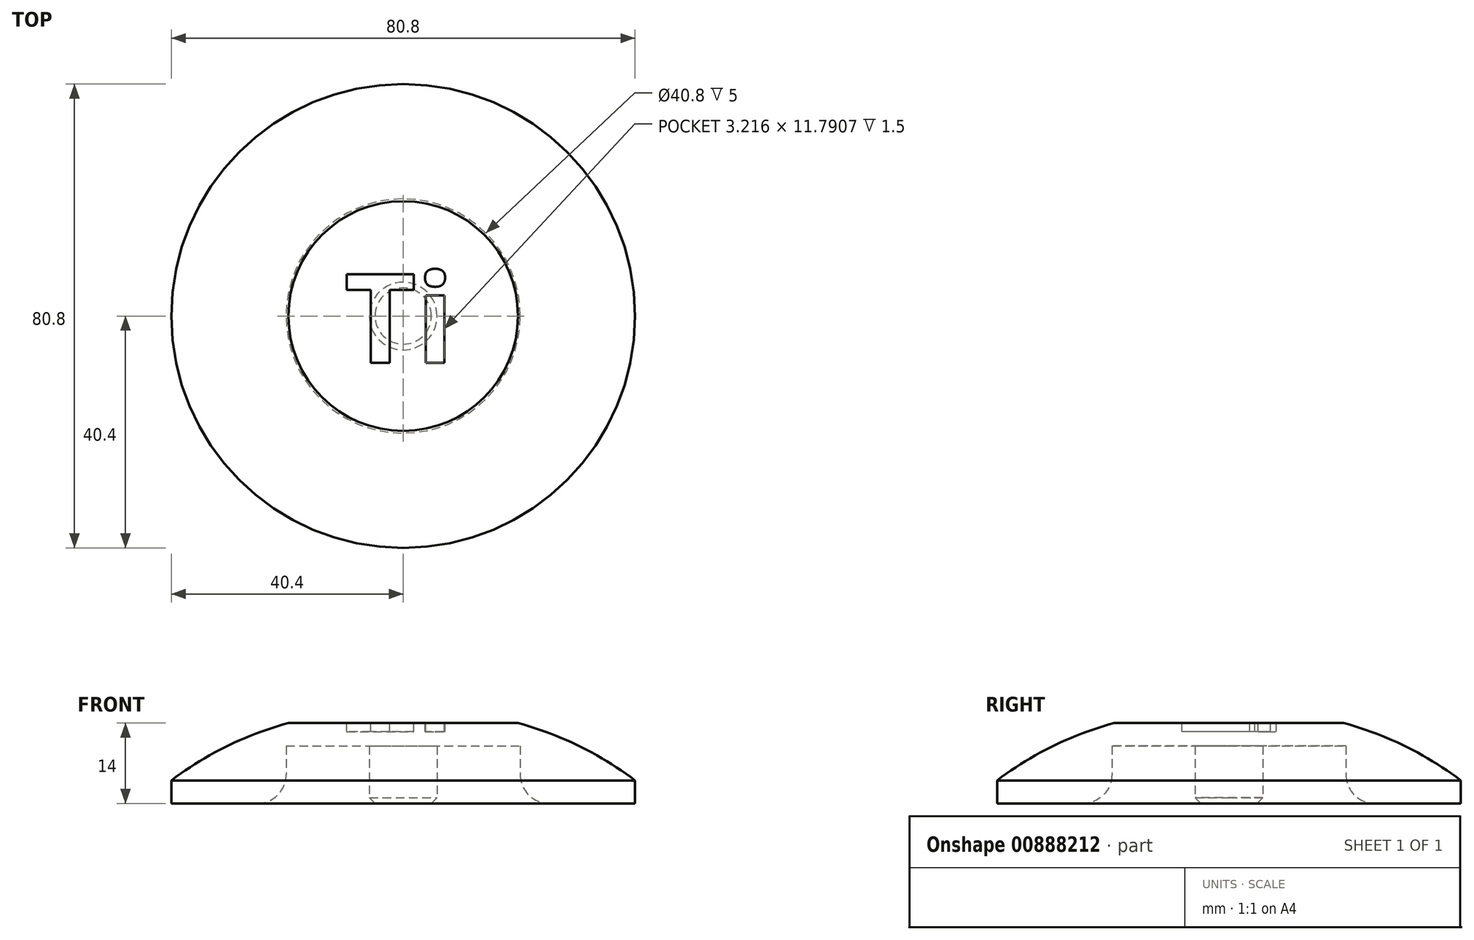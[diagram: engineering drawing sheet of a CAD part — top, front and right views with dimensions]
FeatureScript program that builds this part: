
annotation { "Feature Type Name" : "Feature", "Feature Type Description" : "" }
export const myFeature = defineFeature(function(context is Context, id is Id, definition is map)
    precondition{}
    {
        {
            var Q0;
            Q0=qCreatedBy(makeId("Front.planeOp"),FACE);
            var sketch = newSketch(context, id + "F0", { "sketchPlane" : qUnion([Q0])});
            skLineSegment(sketch, "E0", {"start": v(0, 0) * mm, "end": v(-5.9, 0) * mm});
            skLineSegment(sketch, "E1", {"start": v(-5.9, 0) * mm, "end": v(-5.9, 10) * mm});
            skLineSegment(sketch, "E2", {"start": v(-5.9, 10) * mm, "end": v(-20.4, 10) * mm});
            skLineSegment(sketch, "E3", {"start": v(-20.4, 10) * mm, "end": v(-20.4, 0) * mm});
            skLineSegment(sketch, "E4", {"start": v(-20.4, 0) * mm, "end": v(-40.4, 0) * mm});
            skLineSegment(sketch, "E5", {"start": v(-40.4, 0) * mm, "end": v(-40.4, 4) * mm});
            skLineSegment(sketch, "E6", {"start": v(0, 0) * mm, "end": v(0, 14) * mm});
            skLineSegment(sketch, "E7", {"start": v(0, 14) * mm, "end": v(-20, 14) * mm});
            skArc(sketch, "E8", {"start": v(-20, 14) * mm, "mid": v(-30.68, 9.97) * mm, "end": v(-40.4, 4) * mm});
            skSolve(sketch);
        }
        {
            var Q0;
            Q0=makeQuery(id+"F0.imprint","IMPRINT",FACE,{"disambiguationData":[TD([[makeQuery(id+"F0.imprint","IMPRINT",EDGE,{"derivedFrom":sQuery(id+"F0.wireOp",EDGE,"E0")}),-1.0]])]});
            var Q1;
            Q1=sQuery(id+"F0.wireOp",EDGE,"E6");
            revolve(context, id + "F1", {"surfaceOperationType" : NewSurfaceOperationType.NEW, "entities" : qUnion([Q0]), "axis" : qUnion([Q1]), "revolveType" : RevolveType.FULL});
        }
        {
            var Q0;
            Q0=makeQuery(id+"F1.opRevolve","SWEPT_FACE",FACE,{"disambiguationData":[OSD([sQuery(id+"F0.wireOp",EDGE,"E7")])]});
            var sketch = newSketch(context, id + "F2", { "sketchPlane" : qUnion([Q0])});
            skText(sketch, "E9", { "text": "Ti", "fontName": "OpenSans-Bold.ttf"});
            const initialGuessF2  = {"E9": [-0.01025, -0.00817, 1, 0, 0.01555]};
            skSetInitialGuess(sketch, initialGuessF2);
            skSolve(sketch);
        }
        {
            var Q0;
            Q0 = qSketchRegion(id + "F2", true);
            extrude(context, id + "F3", {"entities" : qUnion([Q0]), "operationType" : NewBodyOperationType.REMOVE, "oppositeDirection" : true, "depth" : 1.5 * mm, "offsetDistance" : 25 * mm});
        }
        {
            var Q0;
            Q0=makeQuery(id+"F1.opRevolve","SWEPT_EDGE",EDGE,{"disambiguationData":[OSD([sQuery(id+"F0.wireOp",EDGE,"E3"),sQuery(id+"F0.wireOp",EDGE,"E4")])]});
            fillet(context, id + "F4", {"entities" : qUnion([Q0]), "radius" : 5 * mm, "tangentPropagation" : true, "allowEdgeOverflow" : false});
        }
        {
            var Q0;
            Q0=makeQuery(id+"F1.opRevolve","SWEPT_EDGE",EDGE,{"disambiguationData":[OSD([sQuery(id+"F0.wireOp",EDGE,"E0"),sQuery(id+"F0.wireOp",EDGE,"E1")])]});
            chamfer(context, id + "F5", {"entities" : qUnion([Q0]), "width" : 1 * mm, "tangentPropagation" : true});
        }
    });
